# Revit family: Trane_TVR_Indoor_High static pressure_4TVA0136(154,192)EF000AA(2nd DC)
name_source: partatom
category: Equipamento mecânico
units: mm (PartAtom-declared; Revit-internal decimal feet)

## family parameters
Com base no plano de trabalho = Não
Compartilhado = Não
Corte com vazios quando carregada = Não
Cota do conector redondo = Utilizar diâmetro
Número OmniClass = 23.75.00.00
Ponto de cálculo do ambiente = Não
Sempre na vertical = Sim
Tipo de parte = Normal
Título OmniClass = Climate Control (HVAC)

## types (3) — shared parameters
Condensation = air
Depth = 905  [stored 2.96916 ft]
Descrição = High efficiency air cooled
Fabricante = TRANE
Gas = R410a
Gas pipe = 28.6
Height = 680  [stored 2.23097 ft]
Installation = Indoor installation
Liquid pipe = 15.9  [stored 0.0521654 ft]
Maximum Fuse Amps = 30 A
Minimum Circuit Amps = 15 A
Power supply = 220-240V ~50/60Hz
Series = ULTRA
URL = https://www.trane.com
Width = 2010  [stored 6.59449 ft]
clearance access behind = 600  [stored 1.9685 ft]
clearance access front = 500  [stored 1.64042 ft]
clearance access left = 600  [stored 1.9685 ft]
clearance access right = 600  [stored 1.9685 ft]

## per-type parameters (varying)
| type | Air  Flow | Cooling Capacity | Cooling Power Input | Heating Capacity | Heating Power Input | Net Weight |
| 4TVA0192EF000AA | 7400/7000/6600/6200/5800/5400/5000 m3/h | 56.00 kW | 2272.000 W | 39.00 kW | 2272.000 W | 218.00 kg |
| 4TVA0136EF000AA | 6500/6150/5800/5450/5100/4750/4400 m3/h | 40.00 kW | 1800.000 W | 45.00 kW | 1800.000 W | 220.00 kg |
| 4TVA0154EF000AA | 6500/6150/5800/5450/5100/4750/4400 m3/h | 45.00 kW | 1800.000 W | 56.00 kW | 1800.000 W | 220.00 kg |

note: column(s) folded — value = type name in every type: Modelo

note: [stored X ft] marks values corroborated as IEEE doubles in the binary element streams (Revit-internal decimal feet)

## geometry (parser evidence)
native form markers: Blend x4, Sweep x9
no freeform markers — native parametric forms only
